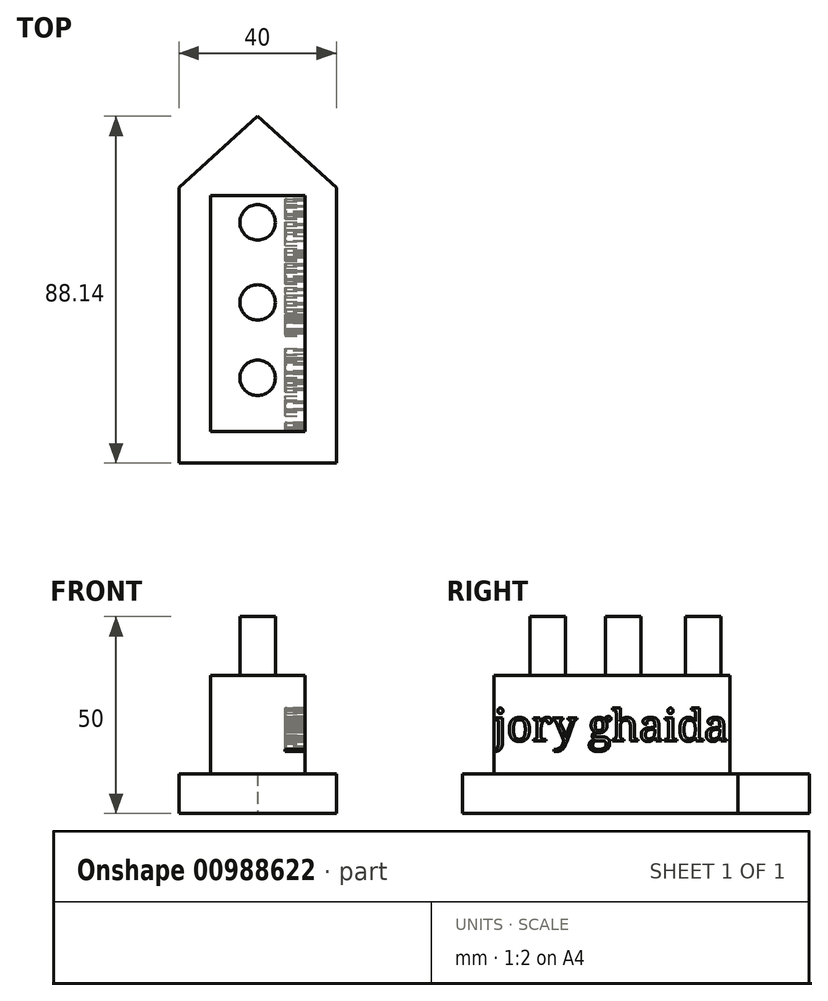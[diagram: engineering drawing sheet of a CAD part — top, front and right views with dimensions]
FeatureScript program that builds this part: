
annotation { "Feature Type Name" : "Feature", "Feature Type Description" : "" }
export const myFeature = defineFeature(function(context is Context, id is Id, definition is map)
    precondition{}
    {
        {
            var Q0;
            Q0=qCreatedBy(makeId("Top.planeOp"),FACE);
            var sketch = newSketch(context, id + "F0", { "sketchPlane" : qUnion([Q0])});
            skLineSegment(sketch, "E0", {"start": v(-20, 25.15) * mm, "end": v(-20, -44.85) * mm});
            skLineSegment(sketch, "E1", {"start": v(-20, -44.85) * mm, "end": v(20, -44.85) * mm});
            skLineSegment(sketch, "E2", {"start": v(20, -44.85) * mm, "end": v(20, 25.15) * mm});
            skLineSegment(sketch, "E3", {"start": v(20, 25.15) * mm, "end": v(0, 43.29) * mm});
            skLineSegment(sketch, "E4", {"start": v(0, 43.29) * mm, "end": v(-20, 25.15) * mm});
            skSolve(sketch);
        }
        {
            var Q0;
            Q0 = qSketchRegion(id + "F0", true);
            extrude(context, id + "F1", {"entities" : qUnion([Q0]), "depth" : 10 * mm, "offsetDistance" : 25 * mm});
        }
        {
            var Q0;
            Q0=makeQuery(id+"F1.opExtrude","CAP_FACE",FACE,{"disambiguationData":[OSD([sQuery(id+"F0.wireOp",EDGE,"E0"),sQuery(id+"F0.wireOp",EDGE,"E1"),sQuery(id+"F0.wireOp",EDGE,"E2"),sQuery(id+"F0.wireOp",EDGE,"E3"),sQuery(id+"F0.wireOp",EDGE,"E4")])],"isStart":false});
            var sketch = newSketch(context, id + "F2", { "sketchPlane" : qUnion([Q0])});
            skLineSegment(sketch, "E5", {"start": v(-12, 23.15) * mm, "end": v(-12, -36.85) * mm});
            skLineSegment(sketch, "E6", {"start": v(-12, -36.85) * mm, "end": v(12, -36.85) * mm});
            skLineSegment(sketch, "E7", {"start": v(12, -36.85) * mm, "end": v(12, 23.15) * mm});
            skLineSegment(sketch, "E8", {"start": v(-12, 23.15) * mm, "end": v(12, 23.15) * mm});
            skSolve(sketch);
        }
        {
            var Q0;
            Q0 = qSketchRegion(id + "F2", true);
            extrude(context, id + "F3", {"entities" : qUnion([Q0]), "operationType" : NewBodyOperationType.ADD, "depth" : 25 * mm, "offsetDistance" : 25 * mm});
        }
        {
            var Q0;
            Q0=makeQuery(id+"F3.opExtrude","CAP_FACE",FACE,{"disambiguationData":[OSD([sQuery(id+"F2.wireOp",EDGE,"E5"),sQuery(id+"F2.wireOp",EDGE,"E6"),sQuery(id+"F2.wireOp",EDGE,"E7"),sQuery(id+"F2.wireOp",EDGE,"E8")])],"isStart":false});
            var sketch = newSketch(context, id + "F4", { "sketchPlane" : qUnion([Q0])});
            skCircle(sketch, "E9", {"center": v(0, 16.3) * mm, "radius": 4.5 * mm});
            skCircle(sketch, "E10", {"center": v(0, -4.04) * mm, "radius": 4.5 * mm});
            skCircle(sketch, "E11", {"center": v(0, -23.2) * mm, "radius": 4.5 * mm});
            skSolve(sketch);
        }
        {
            var Q0;
            Q0 = qSketchRegion(id + "F4", true);
            extrude(context, id + "F5", {"entities" : qUnion([Q0]), "operationType" : NewBodyOperationType.ADD, "depth" : 15 * mm, "offsetDistance" : 25 * mm});
        }
        {
            var Q0;
            Q0=makeQuery(id+"F3.opExtrude","SWEPT_FACE",FACE,{"disambiguationData":[OSD([sQuery(id+"F2.wireOp",EDGE,"E7")])]});
            var sketch = newSketch(context, id + "F6", { "sketchPlane" : qUnion([Q0])});
            skText(sketch, "E12", { "text": "jory ghaida", "fontName": "NotoSerif-Regular.ttf"});
            const initialGuessF6  = {"E12": [-0.03685, 0.01836, 1, 0, 0.00794]};
            skSetInitialGuess(sketch, initialGuessF6);
            skSolve(sketch);
        }
        {
            var Q0;
            Q0 = qSketchRegion(id + "F6", true);
            extrude(context, id + "F7", {"entities" : qUnion([Q0]), "operationType" : NewBodyOperationType.REMOVE, "oppositeDirection" : true, "depth" : 5 * mm, "offsetDistance" : 25 * mm});
        }
    });
